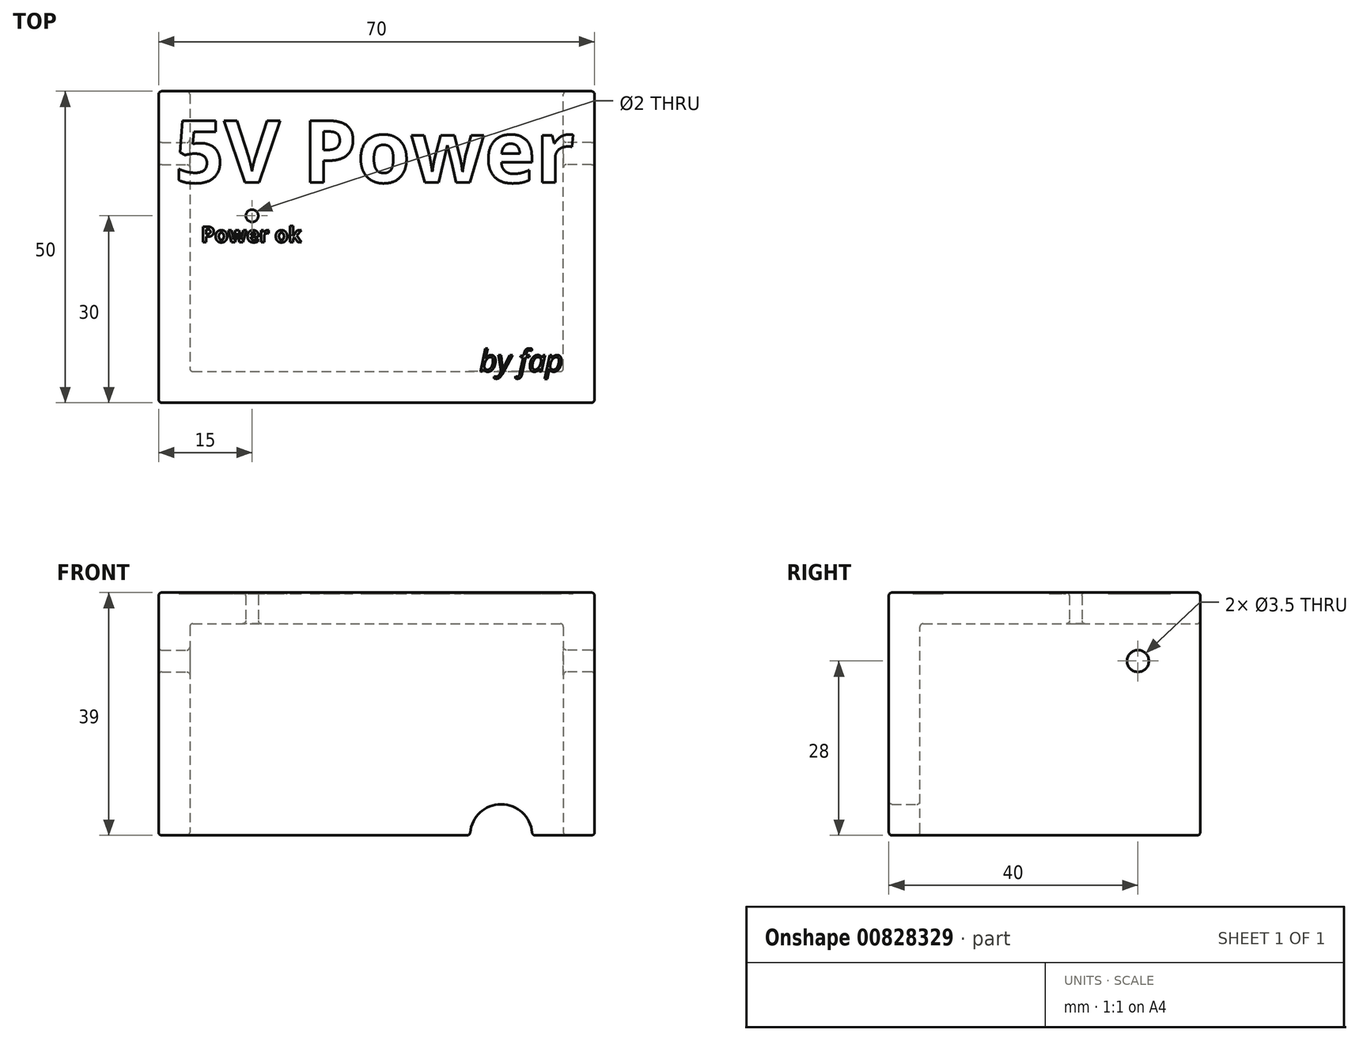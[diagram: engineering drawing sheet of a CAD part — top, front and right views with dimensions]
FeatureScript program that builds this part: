
annotation { "Feature Type Name" : "Feature", "Feature Type Description" : "" }
export const myFeature = defineFeature(function(context is Context, id is Id, definition is map)
    precondition{}
    {
        {
            assignVariable(context, id + "F0", {"name" : "Dicke", "anyValue" : 5});
        }
        {
            var Q0;
            Q0=qCreatedBy(makeId("Front.planeOp"),FACE);
            var sketch = newSketch(context, id + "F1", { "sketchPlane" : qUnion([Q0])});
            skLineSegment(sketch, "E0", {"start": v(-30, 11.86) * mm, "end": v(30, 11.86) * mm});
            skLineSegment(sketch, "E1", {"start": v(30, 11.86) * mm, "end": v(30, -22.14) * mm});
            skLineSegment(sketch, "E2", {"start": v(-30, -22.14) * mm, "end": v(-30, 11.86) * mm});
            skLineSegment(sketch, "E3", {"start": v(0, 11.86) * mm, "end": v(0, -22.14) * mm, "construction": true});
            skLineSegment(sketch, "E4", {"start": v(30, 0) * mm, "end": v(-30, 0) * mm, "construction": true});
            skLineSegment(sketch, "E5", {"start": v(-30, -22.14) * mm, "end": v(15, -22.14) * mm});
            skArc(sketch, "E6", {"start": v(25, -22.14) * mm, "mid": v(20, -17.14) * mm, "end": v(15, -22.14) * mm});
            skLineSegment(sketch, "E7.trimOffspring", {"start": v(25, -22.14) * mm, "end": v(30, -22.14) * mm});
            skLineSegment(sketch, "E8", {"start": v(15, -22.14) * mm, "end": v(25, -22.14) * mm, "construction": true});
            skSolve(sketch);
        }
        {
            var Q0;
            Q0 = qSketchRegion(id + "F1", true);
            extrude(context, id + "F2", {"entities" : qUnion([Q0]), "flatOperationType" : FlatOperationType.REMOVE, "depth" : (getVariable(context, 'Dicke')) * mm, "offsetDistance" : 25 * mm, "domain" : OperationDomain.MODEL});
        }
        {
            var Q0;
            Q0=makeQuery(id+"F2.opExtrude","SWEPT_FACE",FACE,{"disambiguationData":[OSD([sQuery(id+"F1.wireOp",EDGE,"E1")])]});
            var sketch = newSketch(context, id + "F3", { "sketchPlane" : qUnion([Q0])});
            skLineSegment(sketch, "E9", {"start": v(45, 11.86) * mm, "end": v(45, 11.86) * mm});
            skLineSegment(sketch, "E10", {"start": v(-5, 11.86) * mm, "end": v(45, 11.86) * mm});
            skCircle(sketch, "E11", {"center": v(35, 5.86) * mm, "radius": 1.75 * mm});
            skLineSegment(sketch, "E12", {"start": v(-5, -22.14) * mm, "end": v(45, -22.14) * mm});
            skLineSegment(sketch, "E13", {"start": v(45, 11.86) * mm, "end": v(45, -22.14) * mm});
            skSolve(sketch);
        }
        {
            var Q0;
            Q0=makeQuery(id+"F3.imprint","IMPRINT",FACE,{"disambiguationData":[TD([[makeQuery(id+"F3.imprint","IMPRINT",EDGE,{"derivedFrom":sQuery(id+"F3.wireOp",EDGE,"E11")}),-1.0]])]});
            var Q1;
            {var subQ1=sQuery(id+"F1.wireOp",EDGE,"E1");var subQ2=makeQuery(id+"F2.opExtrude","CAP_EDGE",EDGE,{"disambiguationData":[OSD([subQ1])],"isStart":true});Q1=makeQuery(id+"F3.imprint","IMPRINT",FACE,{"disambiguationData":[TD([[makeQuery(id+"F3.imprint","IMPRINT",EDGE,{"derivedFrom":subQ2}),-1.0]])]});}
            extrude(context, id + "F4", {"entities" : qUnion([Q0, Q1]), "operationType" : NewBodyOperationType.ADD, "depth" : (getVariable(context, 'Dicke')) * mm, "offsetDistance" : 25 * mm});
        }
        {
            var Q0;
            Q0=makeQuery(id+"F2.opExtrude","SWEPT_FACE",FACE,{"disambiguationData":[OSD([sQuery(id+"F1.wireOp",EDGE,"E2")])]});
            var sketch = newSketch(context, id + "F5", { "sketchPlane" : qUnion([Q0])});
            skLineSegment(sketch, "E14", {"start": v(5, 11.86) * mm, "end": v(-45, 11.86) * mm});
            skLineSegment(sketch, "E15", {"start": v(-45, 11.86) * mm, "end": v(-45, 11.86) * mm});
            skCircle(sketch, "E16", {"center": v(-35, 5.86) * mm, "radius": 1.75 * mm});
            skLineSegment(sketch, "E17", {"start": v(-45, 11.86) * mm, "end": v(5, 11.86) * mm});
            skLineSegment(sketch, "E18", {"start": v(-45, 11.86) * mm, "end": v(-45, -22.14) * mm});
            skLineSegment(sketch, "E19", {"start": v(-45, -22.14) * mm, "end": v(0, -22.14) * mm});
            skLineSegment(sketch, "E20", {"start": v(-34.64, -22.14) * mm, "end": v(5, -22.14) * mm});
            skSolve(sketch);
        }
        {
            var Q0;
            Q0=makeQuery(id+"F5.imprint","IMPRINT",FACE,{"disambiguationData":[TD([[makeQuery(id+"F5.imprint","IMPRINT",EDGE,{"derivedFrom":sQuery(id+"F5.wireOp",EDGE,"E16")}),-1.0]])]});
            var Q1;
            {var subQ1=sQuery(id+"F1.wireOp",EDGE,"E2");var subQ2=makeQuery(id+"F2.opExtrude","CAP_EDGE",EDGE,{"disambiguationData":[OSD([subQ1])],"isStart":true});Q1=makeQuery(id+"F5.imprint","IMPRINT",FACE,{"disambiguationData":[TD([[makeQuery(id+"F5.imprint","IMPRINT",EDGE,{"derivedFrom":subQ2}),-1.0]])]});}
            extrude(context, id + "F6", {"entities" : qUnion([Q0, Q1]), "operationType" : NewBodyOperationType.ADD, "depth" : (getVariable(context, 'Dicke')) * mm, "offsetDistance" : 25 * mm});
        }
        {
            var Q0;
            Q0=makeQuery(id+"F6.boolean.opBoolean","MERGE",FACE,{"derivedFrom":[makeQuery(id+"F4.boolean.opBoolean","MERGE",FACE,{"derivedFrom":[makeQuery(id+"F2.opExtrude","SWEPT_FACE",FACE,{"disambiguationData":[OSD([sQuery(id+"F1.wireOp",EDGE,"E0")])]}),makeQuery(id+"F4.opExtrude","SWEPT_FACE",FACE,{"disambiguationData":[OSD([sQuery(id+"F3.wireOp",EDGE,"E10")])]})]}),makeQuery(id+"F6.opExtrude","SWEPT_FACE",FACE,{"disambiguationData":[OSD([sQuery(id+"F5.wireOp",EDGE,"E17")])]})]});
            var sketch = newSketch(context, id + "F7", { "sketchPlane" : qUnion([Q0])});
            skLineSegment(sketch, "E21", {"start": v(-30, 45) * mm, "end": v(30, 45) * mm});
            skLineSegment(sketch, "E22", {"start": v(30, 45) * mm, "end": v(30, 0) * mm});
            skLineSegment(sketch, "E23", {"start": v(30, 0) * mm, "end": v(-30, 0) * mm});
            skLineSegment(sketch, "E24", {"start": v(-30, 0) * mm, "end": v(-30, 45) * mm});
            skCircle(sketch, "E25", {"center": v(-20, 25) * mm, "radius": 1 * mm});
            skLineSegment(sketch, "E26", {"start": v(-20, 29.53) * mm, "end": v(-20, 14.74) * mm, "construction": true});
            skSolve(sketch);
        }
        {
            var Q0;
            Q0=makeQuery(id+"F7.imprint","IMPRINT",FACE,{"disambiguationData":[TD([[makeQuery(id+"F7.imprint","IMPRINT",EDGE,{"derivedFrom":sQuery(id+"F7.wireOp",EDGE,"E21")}),-1.0]])]});
            var Q1;
            Q1=makeQuery(id+"F7.imprint","IMPRINT",FACE,{"disambiguationData":[TD([[makeQuery(id+"F7.imprint","IMPRINT",EDGE,{"derivedFrom":sQuery(id+"F7.wireOp",EDGE,"E22")}),-1.0]])]});
            extrude(context, id + "F8", {"entities" : qUnion([Q0, Q1]), "operationType" : NewBodyOperationType.ADD, "depth" : (getVariable(context, 'Dicke')) * mm, "offsetDistance" : 25 * mm});
        }
        {
            var Q0;
            Q0=makeQuery(id+"F8.opExtrude","CAP_FACE",FACE,{"disambiguationData":[OSD([sQuery(id+"F1.wireOp",EDGE,"E0"),sQuery(id+"F1.wireOp",EDGE,"E1"),sQuery(id+"F1.wireOp",EDGE,"E2"),sQuery(id+"F3.wireOp",EDGE,"E10"),sQuery(id+"F3.wireOp",EDGE,"E13"),sQuery(id+"F5.wireOp",EDGE,"E17"),sQuery(id+"F5.wireOp",EDGE,"E18"),sQuery(id+"F7.wireOp",EDGE,"E21")])],"isStart":false});
            var sketch = newSketch(context, id + "F9", { "sketchPlane" : qUnion([Q0])});
            skText(sketch, "E27", { "text": "5V Power", "fontName": "OpenSans-Bold.ttf"});
            skText(sketch, "E28", { "text": "by fap", "fontName": "OpenSans-Italic.ttf"});
            skText(sketch, "E29", { "text": "Power ok", "fontName": "OpenSans-Bold.ttf"});
            const initialGuessF9  = {"E27": [-0.03245, 0.03034, 1, 0, 0.01], "E28": [0.01654, 0, 1, 0, 0.0035], "E29": [-0.02818, 0.02076, 1, 0, 0.0025]};
            skSetInitialGuess(sketch, initialGuessF9);
            skSolve(sketch);
        }
        {
            var Q0;
            Q0 = qSketchRegion(id + "F9", true);
            extrude(context, id + "F10", {"entities" : qUnion([Q0]), "operationType" : NewBodyOperationType.REMOVE, "oppositeDirection" : true, "depth" : 0.2 * mm, "offsetDistance" : 25 * mm});
        }
        {
            var Q0;
            {var subQ0=sQuery(id+"F1.wireOp",EDGE,"E2");var subQ1=sQuery(id+"F1.wireOp",EDGE,"E1");var subQ2=sQuery(id+"F1.wireOp",EDGE,"E0");Q0=makeQuery(id+"F8.boolean.opBoolean","MERGE",FACE,{"derivedFrom":[makeQuery(id+"F6.boolean.opBoolean","MERGE",FACE,{"derivedFrom":[makeQuery(id+"F4.boolean.opBoolean","MERGE",FACE,{"derivedFrom":[makeQuery(id+"F2.opExtrude","CAP_FACE",FACE,{"disambiguationData":[OSD([subQ2,subQ1,subQ0,sQuery(id+"F1.wireOp",EDGE,"E5"),sQuery(id+"F1.wireOp",EDGE,"E6"),sQuery(id+"F1.wireOp",EDGE,"E7.trimOffspring")])],"isStart":false}),makeQuery(id+"F4.opExtrude","SWEPT_FACE",FACE,{"disambiguationData":[OSD([subQ1])]})]}),makeQuery(id+"F6.opExtrude","SWEPT_FACE",FACE,{"disambiguationData":[OSD([subQ0])]})]}),makeQuery(id+"F8.opExtrude","SWEPT_FACE",FACE,{"disambiguationData":[OSD([subQ2,subQ1,subQ0,sQuery(id+"F3.wireOp",EDGE,"E10"),sQuery(id+"F5.wireOp",EDGE,"E17")])]})]});}
            var Q1;
            {var subQ0=sQuery(id+"F5.wireOp",EDGE,"E17");Q1=makeQuery(id+"F8.boolean.opBoolean","MERGE",FACE,{"derivedFrom":[makeQuery(id+"F6.opExtrude","CAP_FACE",FACE,{"disambiguationData":[OSD([sQuery(id+"F1.wireOp",EDGE,"E2"),sQuery(id+"F5.wireOp",EDGE,"E16"),subQ0,sQuery(id+"F5.wireOp",EDGE,"E18"),sQuery(id+"F5.wireOp",EDGE,"E19"),sQuery(id+"F5.wireOp",EDGE,"E20")])],"isStart":false}),makeQuery(id+"F8.opExtrude","SWEPT_FACE",FACE,{"disambiguationData":[OSD([subQ0])]})]});}
            var Q2;
            {var subQ0=sQuery(id+"F3.wireOp",EDGE,"E10");Q2=makeQuery(id+"F8.boolean.opBoolean","MERGE",FACE,{"derivedFrom":[makeQuery(id+"F4.opExtrude","CAP_FACE",FACE,{"disambiguationData":[OSD([sQuery(id+"F1.wireOp",EDGE,"E1"),sQuery(id+"F3.wireOp",EDGE,"E11"),subQ0,sQuery(id+"F3.wireOp",EDGE,"E12"),sQuery(id+"F3.wireOp",EDGE,"E13")])],"isStart":false}),makeQuery(id+"F8.opExtrude","SWEPT_FACE",FACE,{"disambiguationData":[OSD([subQ0])]})]});}
            var Q3;
            Q3=makeQuery(id+"F4.opExtrude","CAP_FACE",FACE,{"disambiguationData":[OSD([sQuery(id+"F1.wireOp",EDGE,"E1"),sQuery(id+"F3.wireOp",EDGE,"E11"),sQuery(id+"F3.wireOp",EDGE,"E10"),sQuery(id+"F3.wireOp",EDGE,"E12"),sQuery(id+"F3.wireOp",EDGE,"E13")])],"isStart":true});
            var Q4;
            Q4=makeQuery(id+"F2.opExtrude","CAP_FACE",FACE,{"disambiguationData":[OSD([sQuery(id+"F1.wireOp",EDGE,"E0"),sQuery(id+"F1.wireOp",EDGE,"E1"),sQuery(id+"F1.wireOp",EDGE,"E2"),sQuery(id+"F1.wireOp",EDGE,"E5"),sQuery(id+"F1.wireOp",EDGE,"E6"),sQuery(id+"F1.wireOp",EDGE,"E7.trimOffspring")])],"isStart":true});
            var Q5;
            Q5=makeQuery(id+"F6.opExtrude","CAP_FACE",FACE,{"disambiguationData":[OSD([sQuery(id+"F1.wireOp",EDGE,"E2"),sQuery(id+"F5.wireOp",EDGE,"E16"),sQuery(id+"F5.wireOp",EDGE,"E17"),sQuery(id+"F5.wireOp",EDGE,"E18"),sQuery(id+"F5.wireOp",EDGE,"E19"),sQuery(id+"F5.wireOp",EDGE,"E20")])],"isStart":true});
            var Q6;
            Q6=makeQuery(id+"F2.opExtrude","SWEPT_EDGE",EDGE,{"disambiguationData":[OSD([sQuery(id+"F1.wireOp",EDGE,"E6"),sQuery(id+"F1.wireOp",EDGE,"E7.trimOffspring")])]});
            var Q7;
            Q7=makeQuery(id+"F2.opExtrude","SWEPT_EDGE",EDGE,{"disambiguationData":[OSD([sQuery(id+"F1.wireOp",EDGE,"E5"),sQuery(id+"F1.wireOp",EDGE,"E6")])]});
            var Q8;
            Q8=makeQuery(id+"F4.opExtrude","SWEPT_EDGE",EDGE,{"disambiguationData":[OSD([sQuery(id+"F3.wireOp",EDGE,"E12"),sQuery(id+"F3.wireOp",EDGE,"E13")])]});
            var Q9;
            Q9=makeQuery(id+"F6.opExtrude","SWEPT_EDGE",EDGE,{"disambiguationData":[OSD([sQuery(id+"F5.wireOp",EDGE,"E18"),sQuery(id+"F5.wireOp",EDGE,"E19")])]});
            var Q10;
            {var subQ0=sQuery(id+"F5.wireOp",EDGE,"E18");var subQ1=sQuery(id+"F3.wireOp",EDGE,"E13");Q10=makeQuery(id+"F8.boolean.opBoolean","MERGE",FACE,{"derivedFrom":[makeQuery(id+"F4.opExtrude","SWEPT_FACE",FACE,{"disambiguationData":[OSD([subQ1])]}),makeQuery(id+"F6.opExtrude","SWEPT_FACE",FACE,{"disambiguationData":[OSD([subQ0])]}),makeQuery(id+"F8.opExtrude","SWEPT_FACE",FACE,{"disambiguationData":[OSD([sQuery(id+"F3.wireOp",EDGE,"E10"),subQ1,sQuery(id+"F5.wireOp",EDGE,"E17"),subQ0,sQuery(id+"F7.wireOp",EDGE,"E21")])]})]});}
            var Q11;
            Q11=makeQuery(id+"F8.opExtrude","CAP_EDGE",EDGE,{"disambiguationData":[OSD([sQuery(id+"F7.wireOp",EDGE,"E25")])],"isStart":false});
            var Q12;
            Q12=makeQuery(id+"F8.opExtrude","CAP_EDGE",EDGE,{"disambiguationData":[OSD([sQuery(id+"F7.wireOp",EDGE,"E25")])],"isStart":true});
            fillet(context, id + "F11", {"entities" : qUnion([Q0, Q1, Q2, Q3, Q4, Q5, Q6, Q7, Q8, Q9, Q10, Q11, Q12]), "radius" : 0.5 * mm, "tangentPropagation" : true, "allowEdgeOverflow" : false});
        }
    });
